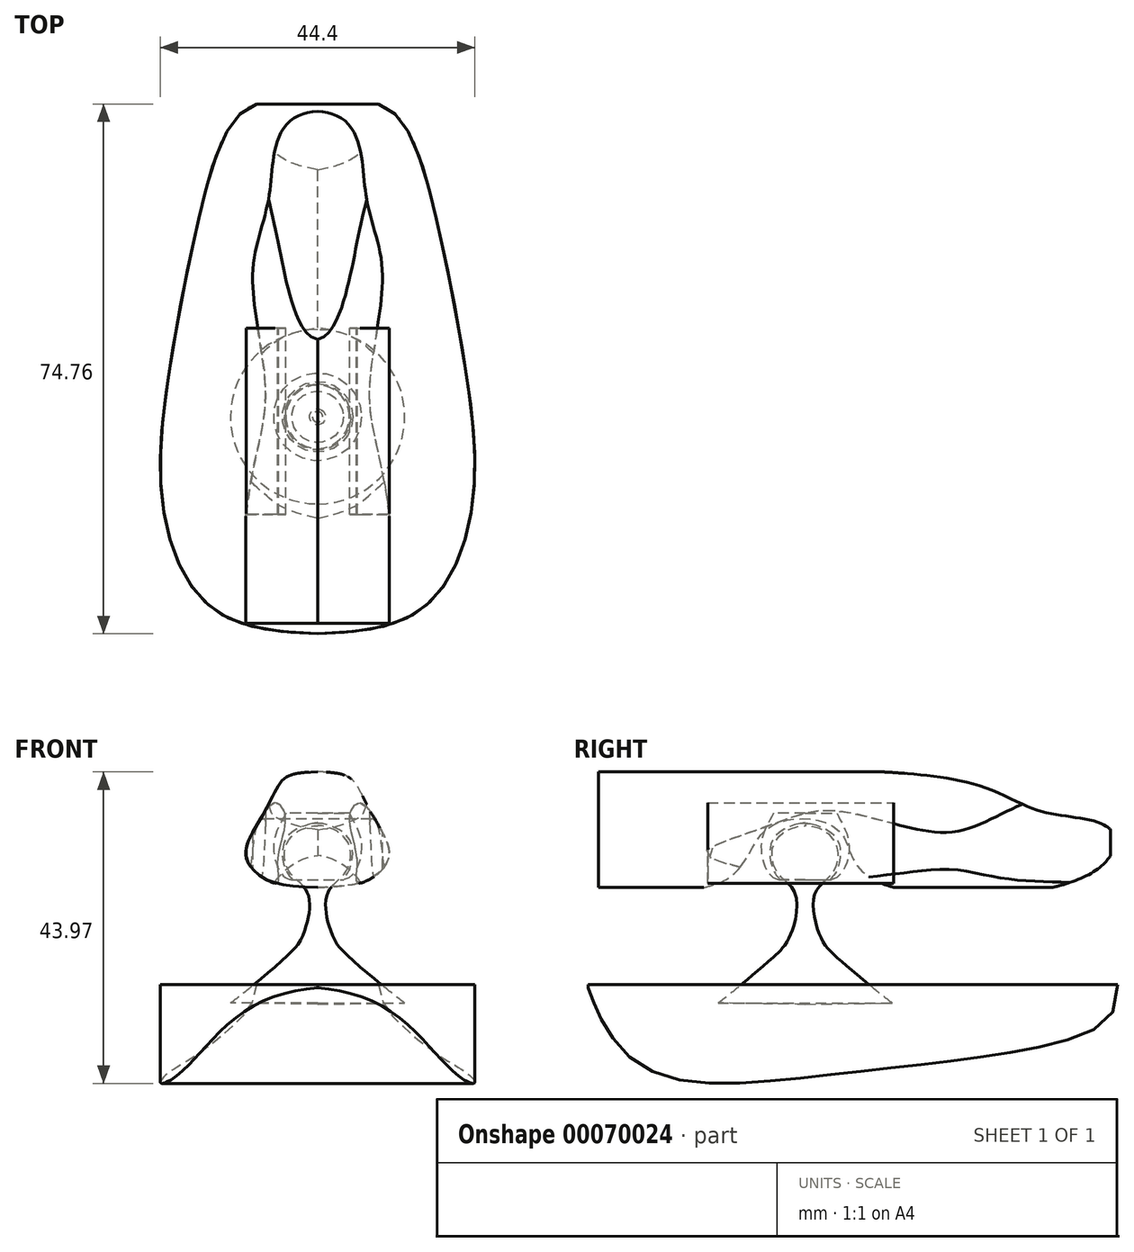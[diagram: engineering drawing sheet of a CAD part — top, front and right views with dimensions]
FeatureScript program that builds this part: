
annotation { "Feature Type Name" : "Feature", "Feature Type Description" : "" }
export const myFeature = defineFeature(function(context is Context, id is Id, definition is map)
    precondition{}
    {
        {
            var Q0;
            Q0=qCreatedBy(makeId("Top.planeOp"),FACE);
            var sketch = newSketch(context, id + "F0", { "sketchPlane" : qUnion([Q0])});
            skFitSpline(sketch, "E0", {"points": [v(0, 37.16) * mm, v(11.1, 35.03) * mm, v(17.08, 19.01) * mm, v(20.75, 0) * mm, v(21.9, -19.6) * mm, v(16.12, -33.5) * mm, v(0, -38.18) * mm], "startDerivative": vector(118.91, 1.45) * mm, "endDerivative": vector(-142.68, -4.6) * mm});
            skFitSpline(sketch, "E1.MirrorCS", {"points": [v(0, 37.16) * mm, v(-11.1, 35.03) * mm, v(-17.08, 19.01) * mm, v(-20.75, 0) * mm, v(-21.9, -19.6) * mm, v(-16.12, -33.5) * mm, v(0, -38.18) * mm], "startDerivative": vector(-118.91, 1.45) * mm, "endDerivative": vector(142.68, -4.6) * mm});
            skSolve(sketch);
        }
        {
            var Q0;
            Q0=qCreatedBy(makeId("Right.planeOp"),FACE);
            var sketch = newSketch(context, id + "F1", { "sketchPlane" : qUnion([Q0])});
            skFitSpline(sketch, "E2", {"points": [v(-38.33, 0) * mm, v(-27.7, -12.84) * mm, v(0, -12.26) * mm, v(34.46, -5.5) * mm, v(36.58, 0) * mm], "startDerivative": vector(32.79, -96.67) * mm, "endDerivative": vector(1.74, 42.53) * mm});
            skFitSpline(sketch, "E3", {"points": [v(36.58, 0) * mm, v(-38.33, 0) * mm], "startDerivative": vector(-74.9, 0) * mm, "endDerivative": vector(-74.9, 0) * mm});
            skSolve(sketch);
        }
        {
            var Q0;
            Q0=qCreatedBy(makeId("Right.planeOp"),FACE);
            var sketch = newSketch(context, id + "F2", { "sketchPlane" : qUnion([Q0])});
            skFitSpline(sketch, "E4", {"points": [v(4.73, -2.6) * mm, v(-3.18, 3.96) * mm, v(-5.4, 6.78) * mm, v(-6.22, 12.76) * mm, v(-3.56, 16) * mm, v(-3.42, 20.3) * mm, v(-7.57, 22.43) * mm], "startDerivative": vector(-38.6, 29.37) * mm, "endDerivative": vector(-29.2, 0) * mm});
            skLineSegment(sketch, "E5", {"start": v(-7.57, 22.43) * mm, "end": v(-7.57, -2.78) * mm});
            skLineSegment(sketch, "E6", {"start": v(-7.57, -2.78) * mm, "end": v(4.73, -2.6) * mm});
            skSolve(sketch);
        }
        {
            var Q0;
            Q0=qCreatedBy(makeId("Right.planeOp"),FACE);
            var sketch = newSketch(context, id + "F3", { "sketchPlane" : qUnion([Q0])});
            skFitSpline(sketch, "E7", {"points": [v(-3.1, 24.18) * mm, v(-1.38, 19.8) * mm, v(-2.8, 15.33) * mm, v(-3.94, 14.85) * mm, v(-3.39, 15.62) * mm, v(-2.8, 19.93) * mm, v(-7.57, 22.85) * mm], "startDerivative": vector(11.32, -21.55) * mm, "endDerivative": vector(-33.98, 4.84) * mm});
            skLineSegment(sketch, "E8", {"start": v(-7.57, 24.18) * mm, "end": v(-7.57, 22.85) * mm});
            skLineSegment(sketch, "E9", {"start": v(-7.57, 24.18) * mm, "end": v(-3.1, 24.18) * mm});
            skLineSegment(sketch, "E10", {"start": v(-7.57, 22.85) * mm, "end": v(-6.84, 22.72) * mm});
            skSolve(sketch);
        }
        {
            var Q0;
            Q0=qCreatedBy(makeId("Right.planeOp"),FACE);
            var sketch = newSketch(context, id + "F4", { "sketchPlane" : qUnion([Q0])});
            skLineSegment(sketch, "E11", {"start": v(-38.45, 13.25) * mm, "end": v(-38.42, 30.44) * mm});
            skFitSpline(sketch, "E12", {"points": [v(-38.45, 13.25) * mm, v(-18.16, 15.2) * mm, v(-13.46, 21.53) * mm, v(-7.45, 23.4) * mm, v(-2.34, 21.2) * mm, v(1.56, 15.11) * mm, v(32.89, 15.76) * mm, v(35.56, 21.85) * mm, v(26.07, 24.37) * mm, v(14.06, 28.83) * mm, v(-38.42, 30.44) * mm], "startDerivative": vector(199.25, -4.86) * mm, "endDerivative": vector(-172.1, 7.37) * mm});
            skSolve(sketch);
        }
        {
            var Q0;
            Q0=makeQuery(id+"F2.imprint","IMPRINT",FACE,{"disambiguationData":[TD([[makeQuery(id+"F2.imprint","IMPRINT",EDGE,{"derivedFrom":sQuery(id+"F2.wireOp",EDGE,"E4")}),1.0]])]});
            var Q1;
            Q1=sQuery(id+"F2.wireOp",EDGE,"E4");
            var Q2;
            Q2=sQuery(id+"F2.wireOp",EDGE,"E5");
            revolve(context, id + "F5", {"entities" : qUnion([Q0]), "surfaceEntities" : qUnion([Q1]), "axis" : qUnion([Q2]), "revolveType" : RevolveType.FULL});
        }
        {
            var Q0;
            Q0 = qSketchRegion(id + "F0", true);
            extrude(context, id + "F6", {"entities" : qUnion([Q0]), "oppositeDirection" : true, "depth" : 25.4 * mm});
        }
        {
            var Q0;
            Q0 = qSketchRegion(id + "F1", true);
            extrude(context, id + "F7", {"entities" : qUnion([Q0]), "endBound" : BoundingType.SYMMETRIC, "oppositeDirection" : true, "depth" : 76.2 * mm});
        }
        {
            var Q0;
            Q0=makeQuery(id+"F6.opExtrude","SWEPT_BODY",BODY,{"disambiguationData":[OSD([sQuery(id+"F0.wireOp",EDGE,"E0"),sQuery(id+"F0.wireOp",EDGE,"E1.MirrorCS")])]});
            var Q1;
            Q1=makeQuery(id+"F7.opExtrude","SWEPT_BODY",BODY,{"disambiguationData":[OSD([sQuery(id+"F1.wireOp",EDGE,"E2"),sQuery(id+"F1.wireOp",EDGE,"E3")])]});
            booleanBodies(context, id + "F8", {"operationType" : BooleanOperationType.INTERSECTION, "tools" : qUnion([Q0, Q1])});
        }
        {
            var Q0;
            Q0 = qSketchRegion(id + "F3", true);
            var Q1;
            Q1=sQuery(id+"F3.wireOp",EDGE,"E8");
            revolve(context, id + "F9", {"entities" : qUnion([Q0]), "axis" : qUnion([Q1]), "revolveType" : RevolveType.FULL});
        }
        {
            var Q0;
            Q0=makeQuery(id+"F4.imprint","IMPRINT",FACE,{"disambiguationData":[TD([[makeQuery(id+"F4.imprint","IMPRINT",EDGE,{"derivedFrom":sQuery(id+"F4.wireOp",EDGE,"E11")}),-1.0]])]});
            extrude(context, id + "F10", {"entities" : qUnion([Q0]), "endBound" : BoundingType.SYMMETRIC, "depth" : 25.4 * mm});
        }
        {
            var Q0;
            Q0=qCreatedBy(makeId("Top.planeOp"),FACE);
            var sketch = newSketch(context, id + "F11", { "sketchPlane" : qUnion([Q0])});
            skFitSpline(sketch, "E13", {"points": [v(0, 35.54) * mm, v(6.76, 24.18) * mm, v(9.14, 13) * mm, v(7.38, -3.21) * mm, v(8.68, -13.03) * mm, v(11.1, -36.73) * mm], "startDerivative": vector(104.4, -5.14) * mm, "endDerivative": vector(3.55, -146.5) * mm});
            skLineSegment(sketch, "E14", {"start": v(11.1, -36.73) * mm, "end": v(0, -36.73) * mm});
            skLineSegment(sketch, "E15", {"start": v(0, -36.73) * mm, "end": v(0, 35.54) * mm});
            skFitSpline(sketch, "E16.MirrorCS", {"points": [v(0, 35.54) * mm, v(-6.76, 24.18) * mm, v(-9.14, 13) * mm, v(-7.38, -3.21) * mm, v(-8.68, -13.03) * mm, v(-11.1, -36.73) * mm], "startDerivative": vector(-104.4, -5.14) * mm, "endDerivative": vector(-3.55, -146.5) * mm});
            skLineSegment(sketch, "E17.MirrorCS", {"start": v(-11.1, -36.73) * mm, "end": v(0, -36.73) * mm});
            skSolve(sketch);
        }
        {
            var Q0;
            Q0=qCreatedBy(makeId("Front.planeOp"),FACE);
            var sketch = newSketch(context, id + "F12", { "sketchPlane" : qUnion([Q0])});
            skFitSpline(sketch, "E18", {"points": [v(0, 30.03) * mm, v(5.37, 28.35) * mm, v(7.7, 23.97) * mm, v(10.14, 18.5) * mm, v(7.56, 15.02) * mm, v(0, 13.7) * mm], "startDerivative": vector(52.55, -0.5) * mm, "endDerivative": vector(-45.14, -2.39) * mm});
            skFitSpline(sketch, "E19.MirrorCS", {"points": [v(0, 30.03) * mm, v(-5.37, 28.35) * mm, v(-7.7, 23.97) * mm, v(-10.14, 18.5) * mm, v(-7.56, 15.02) * mm, v(0, 13.7) * mm], "startDerivative": vector(-52.55, -0.5) * mm, "endDerivative": vector(45.14, -2.39) * mm});
            skSolve(sketch);
        }
        {
            var Q0;
            Q0=qCreatedBy(makeId("Front.planeOp"),FACE);
            var sketch = newSketch(context, id + "F13", { "sketchPlane" : qUnion([Q0])});
            skFitSpline(sketch, "E20", {"points": [v(6.02, 25.65) * mm, v(8.98, 21.76) * mm, v(10.08, 19) * mm, v(9.52, 16.77) * mm, v(7.14, 14.76) * mm, v(5.6, 14.42) * mm, v(5.6, 17.57) * mm, v(4.53, 23.73) * mm, v(6.02, 25.65) * mm]});
            skFitSpline(sketch, "E21.MirrorC", {"points": [v(-6.02, 25.65) * mm, v(-8.98, 21.76) * mm, v(-10.08, 19) * mm, v(-9.52, 16.77) * mm, v(-7.14, 14.76) * mm, v(-5.6, 14.42) * mm, v(-5.6, 17.57) * mm, v(-4.53, 23.73) * mm, v(-6.02, 25.65) * mm]});
            skSolve(sketch);
        }
        {
            var Q0;
            Q0 = qSketchRegion(id + "F13", true);
            extrude(context, id + "F14", {"entities" : qUnion([Q0]), "depth" : 26.27 * mm});
        }
        {
            var Q0;
            Q0=makeQuery(id+"F14.opExtrude","SWEPT_BODY",BODY,{"disambiguationData":[OSD([sQuery(id+"F13.wireOp",EDGE,"E20")])]});
            var Q1;
            Q1=makeQuery(id+"F14.opExtrude","SWEPT_BODY",BODY,{"disambiguationData":[OSD([sQuery(id+"F13.wireOp",EDGE,"E21.MirrorC")])]});
            transform(context, id + "F15", {"entities" : qUnion([Q0, Q1]), "transformType" : TransformType.TRANSLATION_3D, "dx" : 0 * mm, "dy" : 4.95 * mm, "dz" : 0 * mm, "makeCopy" : false});
        }
        {
            var Q0;
            Q0 = qSketchRegion(id + "F12", true);
            extrude(context, id + "F16", {"entities" : qUnion([Q0]), "endBound" : BoundingType.SYMMETRIC, "depth" : 76.2 * mm});
        }
        {
            var Q0;
            Q0=makeQuery(id+"F10.opExtrude","SWEPT_BODY",BODY,{"disambiguationData":[OSD([sQuery(id+"F4.wireOp",EDGE,"E11"),sQuery(id+"F4.wireOp",EDGE,"E12")])]});
            var Q1;
            Q1=makeQuery(id+"F16.opExtrude","SWEPT_BODY",BODY,{"disambiguationData":[OSD([sQuery(id+"F12.wireOp",EDGE,"E18"),sQuery(id+"F12.wireOp",EDGE,"E19.MirrorCS")])]});
            booleanBodies(context, id + "F17", {"operationType" : BooleanOperationType.INTERSECTION, "tools" : qUnion([Q0, Q1])});
        }
        {
            var Q0;
            Q0 = qSketchRegion(id + "F11", true);
            extrude(context, id + "F18", {"entities" : qUnion([Q0]), "endBound" : BoundingType.SYMMETRIC, "depth" : 68.53 * mm});
        }
        {
            var Q0;
            Q0=makeQuery(id+"F17.opBoolean","INTERSECT",BODY,{"derivedFrom":[makeQuery(id+"F10.opExtrude","SWEPT_BODY",BODY,{"disambiguationData":[OSD([sQuery(id+"F4.wireOp",EDGE,"E11"),sQuery(id+"F4.wireOp",EDGE,"E12")])]}),makeQuery(id+"F16.opExtrude","SWEPT_BODY",BODY,{"disambiguationData":[OSD([sQuery(id+"F12.wireOp",EDGE,"E18"),sQuery(id+"F12.wireOp",EDGE,"E19.MirrorCS")])]})]});
            var Q1;
            Q1=makeQuery(id+"F18.opExtrude","SWEPT_BODY",BODY,{"disambiguationData":[OSD([sQuery(id+"F11.wireOp",EDGE,"E13"),sQuery(id+"F11.wireOp",EDGE,"E14"),sQuery(id+"F11.wireOp",EDGE,"E16.MirrorCS"),sQuery(id+"F11.wireOp",EDGE,"E17.MirrorCS")])]});
            booleanBodies(context, id + "F19", {"operationType" : BooleanOperationType.INTERSECTION, "tools" : qUnion([Q0, Q1])});
        }
    });
